# Revit family: Sanitary_Accessories_hansgrohe_Joleena-Soap-lotion-dispenser-04796000_
name_source: partatom
category: Furniture
revit_build: Autodesk Revit 2015 (Build: 20140903_1530(x64)
units: mm (PartAtom-declared; Revit-internal decimal feet)

## types (1)
- Chrome 000
    BIMobject category = Accessories
    BIMobject category code = sanitary-accessories1
    BIMobject main category = Sanitary
    BIMobject main category code = sanitary
    BOSUseNativeGeometries = 1
    Brand url = http://www.hansgrohe-int.com
    Default Elevation = 4' - 0"
    Design country = Germany
    Edition number = 1
    GTIN code = https://4059625203712
    IFC Classification = Sanitary Terminal
    Installation instructions = https://www.hansgrohe-usa.com
    Manufacturer country = Germany
    Manufacturer name = hansgrohe
    Masterformat 2014 Code = 01 52 19
    Masterformat 2014 Description = Sanitary Facilities
    Material main = Chrome
    NBS Reference Code = 31-75
    NBS Reference Description = Sanitary Accessories
    OmniClass Code = 23-21 43 15 23
    OmniClass Description = Lotion Dispensers
    Product Guid = 48718b7b-8d76-46b6-aaa3-d14025f94df9
    Product SKU = 04796000
    Product data url = https://bimobject.com
    Product family = Joleena
    Product group = Sink accessoires
    Product name = Joleena Soap-/ lotion dispenser 04796000
    Product url = https://www.hansgrohe-usa.com
    QR code = http://bimobject.com
    Technical description = https://www.hansgrohe-usa.com
    UNSPSC Code = 301815
    Uniclass 1.4 Code = L8244
    Uniclass 1.4 Description = Sanitary dispensers
    Uniclass 2.0 Code = PR-31-75
    Uniclass 2.0 Description = Sanitary Accessories
    Uniclass 2015 Code = Pr_40_70_22
    Uniclass 2015 Name = Dispensers and acceptance units
    Uniformat II Code = E1090
    Uniformat II Description = Other Equipment

## geometry (parser evidence)
native form markers: Sweep x3
no freeform markers — native parametric forms only
